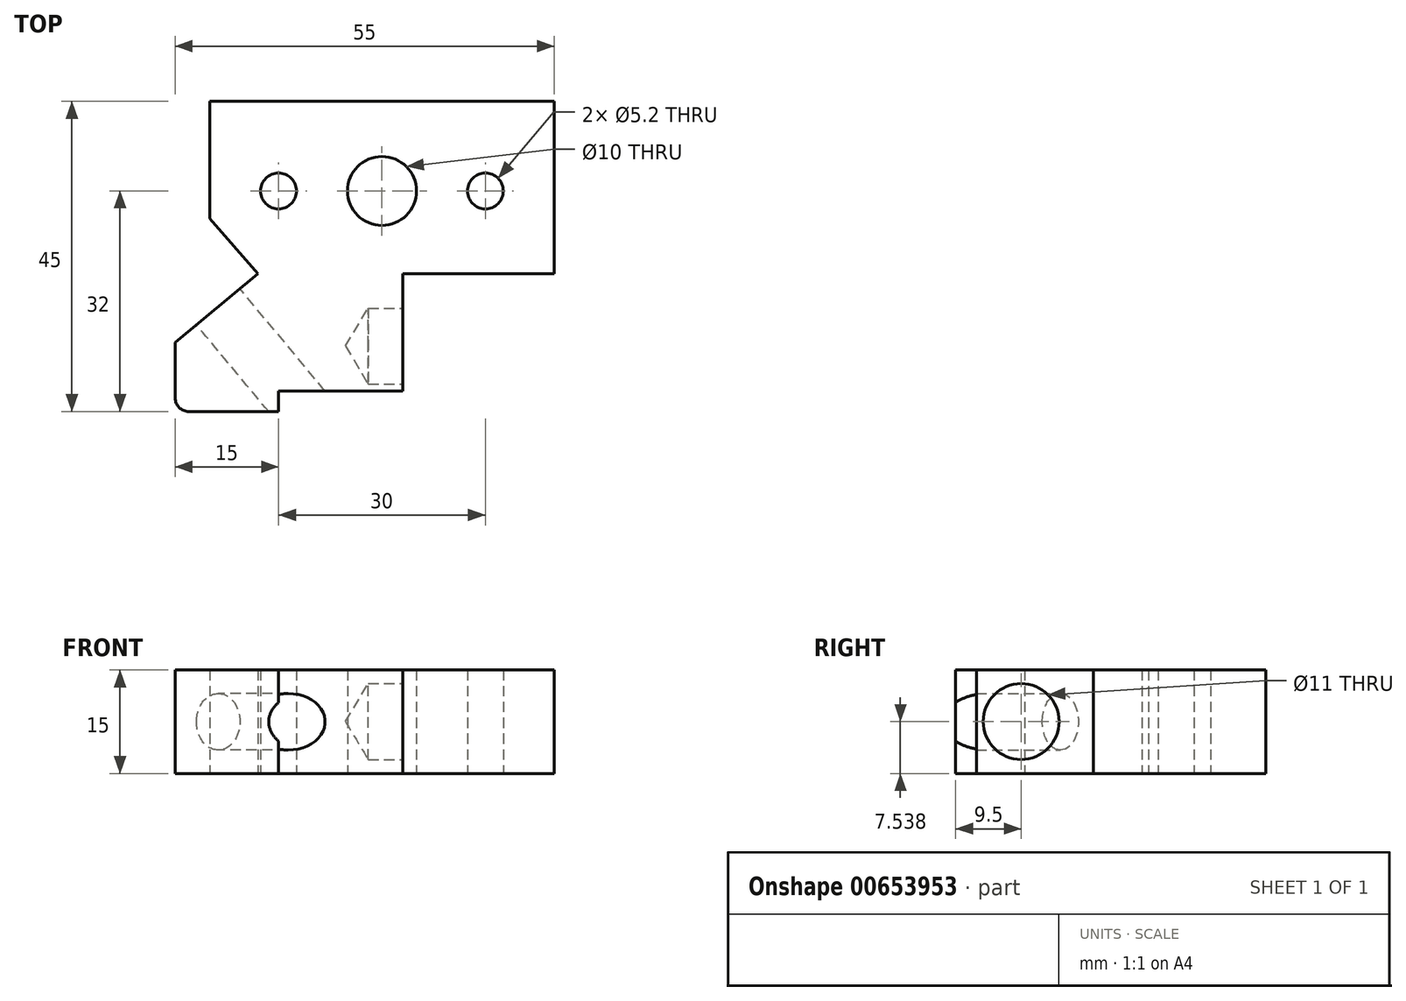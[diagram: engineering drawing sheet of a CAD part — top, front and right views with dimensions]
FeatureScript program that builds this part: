
annotation { "Feature Type Name" : "Feature", "Feature Type Description" : "" }
export const myFeature = defineFeature(function(context is Context, id is Id, definition is map)
    precondition{}
    {
        {
            var Q0;
            Q0=qCreatedBy(makeId("Top.planeOp"),FACE);
            var sketch = newSketch(context, id + "F0", { "sketchPlane" : qUnion([Q0])});
            skLineSegment(sketch, "E0.bottom", {"start": v(-25, 13) * mm, "end": v(25, 13) * mm});
            skLineSegment(sketch, "E0.left", {"start": v(-25, 13) * mm, "end": v(-25, -4) * mm});
            skLineSegment(sketch, "E0.right", {"start": v(25, 13) * mm, "end": v(25, -12) * mm});
            skPoint(sketch, "E1.end.orphan", {"position": v(0, -23.39) * mm});
            skLineSegment(sketch, "E2", {"start": v(25, -12) * mm, "end": v(3, -12) * mm});
            skLineSegment(sketch, "E3", {"start": v(3, -12) * mm, "end": v(3, -29) * mm});
            skLineSegment(sketch, "E4", {"start": v(3, -29) * mm, "end": v(-15, -29) * mm});
            skLineSegment(sketch, "E5", {"start": v(-15, -29) * mm, "end": v(-15, -32) * mm});
            skLineSegment(sketch, "E6", {"start": v(-15, -32) * mm, "end": v(-28, -32) * mm});
            skLineSegment(sketch, "E7", {"start": v(-30, -30) * mm, "end": v(-30, -22) * mm});
            skLineSegment(sketch, "E8", {"start": v(-30, -22) * mm, "end": v(-18, -12) * mm});
            skLineSegment(sketch, "E9", {"start": v(-18, -12) * mm, "end": v(-25, -4) * mm});
            skPoint(sketch, "E10", {"position": v(15, 0) * mm});
            skPoint(sketch, "E11", {"position": v(0, 0) * mm});
            skPoint(sketch, "E12", {"position": v(-15, 0) * mm});
            skPoint(sketch, "E13.visualSharp", {"position": v(-30, -32) * mm});
            skArc(sketch, "E13.filletArc", {"start": v(-30, -30) * mm, "mid": v(-29.41, -31.41) * mm, "end": v(-28, -32) * mm});
            skSolve(sketch);
        }
        {
            var Q0;
            Q0=makeQuery(id+"F0.imprint","IMPRINT",FACE,{"disambiguationData":[TD([[makeQuery(id+"F0.imprint","IMPRINT",EDGE,{"derivedFrom":sQuery(id+"F0.wireOp",EDGE,"E0.bottom")}),-1.0]])]});
            extrude(context, id + "F1", {"entities" : qUnion([Q0]), "depth" : 15 * mm, "offsetDistance" : 25 * mm});
        }
        {
            var Q0;
            Q0=sQuery(id+"F0.wireOp",VERTEX,"E12");
            var Q1;
            Q1=sQuery(id+"F0.wireOp",VERTEX,"E10");
            var Q2;
            Q2=makeQuery(id+"F1.opExtrude","SWEPT_BODY",BODY,{"disambiguationData":[OSD([sQuery(id+"F0.wireOp",EDGE,"E0.bottom"),sQuery(id+"F0.wireOp",EDGE,"E0.left"),sQuery(id+"F0.wireOp",EDGE,"E0.right"),sQuery(id+"F0.wireOp",EDGE,"E2"),sQuery(id+"F0.wireOp",EDGE,"E3"),sQuery(id+"F0.wireOp",EDGE,"E4"),sQuery(id+"F0.wireOp",EDGE,"E5"),sQuery(id+"F0.wireOp",EDGE,"E6"),sQuery(id+"F0.wireOp",EDGE,"E7"),sQuery(id+"F0.wireOp",EDGE,"E8"),sQuery(id+"F0.wireOp",EDGE,"E9")])]});
            hole(context, id + "F2", {"style" : HoleStyle.SIMPLE, "endStyle" : HoleEndStyle.THROUGH, "oppositeDirection" : true, "holeDiameter" : 5.2 * mm, "majorDiameter" : 5 * mm, "isTappedThrough" : true, "tappedDepth" : 12 * mm, "tapClearance" : 3, "locations" : qUnion([Q0, Q1]), "scope" : qUnion([Q2])});
        }
        {
            var Q0;
            Q0=sQuery(id+"F0.wireOp",VERTEX,"E11");
            var Q1;
            Q1=makeQuery(id+"F1.opExtrude","SWEPT_BODY",BODY,{"disambiguationData":[OSD([sQuery(id+"F0.wireOp",EDGE,"E0.bottom"),sQuery(id+"F0.wireOp",EDGE,"E0.left"),sQuery(id+"F0.wireOp",EDGE,"E0.right"),sQuery(id+"F0.wireOp",EDGE,"E2"),sQuery(id+"F0.wireOp",EDGE,"E3"),sQuery(id+"F0.wireOp",EDGE,"E4"),sQuery(id+"F0.wireOp",EDGE,"E5"),sQuery(id+"F0.wireOp",EDGE,"E6"),sQuery(id+"F0.wireOp",EDGE,"E7"),sQuery(id+"F0.wireOp",EDGE,"E8"),sQuery(id+"F0.wireOp",EDGE,"E9")])]});
            hole(context, id + "F3", {"style" : HoleStyle.SIMPLE, "endStyle" : HoleEndStyle.THROUGH, "oppositeDirection" : true, "holeDiameter" : 10 * mm, "majorDiameter" : 5 * mm, "isTappedThrough" : true, "tappedDepth" : 12 * mm, "tapClearance" : 3, "locations" : qUnion([Q0]), "scope" : qUnion([Q1])});
        }
        {
            var Q0;
            Q0=makeQuery(id+"F1.opExtrude","SWEPT_FACE",FACE,{"disambiguationData":[OSD([sQuery(id+"F0.wireOp",EDGE,"E8")])]});
            var sketch = newSketch(context, id + "F4", { "sketchPlane" : qUnion([Q0])});
            skPoint(sketch, "E14", {"position": v(29.01, 7.5) * mm});
            skSolve(sketch);
        }
        {
            var Q0;
            Q0=sQuery(id+"F4.wireOp",VERTEX,"E14");
            var Q1;
            Q1=makeQuery(id+"F1.opExtrude","SWEPT_BODY",BODY,{"disambiguationData":[OSD([sQuery(id+"F0.wireOp",EDGE,"E0.bottom"),sQuery(id+"F0.wireOp",EDGE,"E0.left"),sQuery(id+"F0.wireOp",EDGE,"E0.right"),sQuery(id+"F0.wireOp",EDGE,"E2"),sQuery(id+"F0.wireOp",EDGE,"E3"),sQuery(id+"F0.wireOp",EDGE,"E4"),sQuery(id+"F0.wireOp",EDGE,"E5"),sQuery(id+"F0.wireOp",EDGE,"E6"),sQuery(id+"F0.wireOp",EDGE,"E7"),sQuery(id+"F0.wireOp",EDGE,"E8"),sQuery(id+"F0.wireOp",EDGE,"E9")])]});
            hole(context, id + "F5", {"style" : HoleStyle.SIMPLE, "endStyle" : HoleEndStyle.THROUGH, "standardTappedOrClearance" : lookupTablePath({ "standard" : "ISO", "size" : "8.2", "type" : "Drilled" }), "standardBlindInLast" : lookupTablePath({ "standard" : "ISO", "size" : "8.2", "type" : "Drilled" }), "holeDiameter" : 8.2 * mm, "majorDiameter" : 5 * mm, "isTappedThrough" : true, "tappedDepth" : 12 * mm, "tapClearance" : 3, "locations" : qUnion([Q0]), "scope" : qUnion([Q1])});
        }
        {
            var Q0;
            Q0=makeQuery(id+"F1.opExtrude","SWEPT_FACE",FACE,{"disambiguationData":[OSD([sQuery(id+"F0.wireOp",EDGE,"E3")])]});
            var sketch = newSketch(context, id + "F6", { "sketchPlane" : qUnion([Q0])});
            skPoint(sketch, "E15", {"position": v(-22.5, 7.54) * mm});
            skSolve(sketch);
        }
        {
            var Q0;
            Q0=sQuery(id+"F6.wireOp",VERTEX,"E15");
            var Q1;
            Q1=makeQuery(id+"F1.opExtrude","SWEPT_BODY",BODY,{"disambiguationData":[OSD([sQuery(id+"F0.wireOp",EDGE,"E0.bottom"),sQuery(id+"F0.wireOp",EDGE,"E0.left"),sQuery(id+"F0.wireOp",EDGE,"E0.right"),sQuery(id+"F0.wireOp",EDGE,"E2"),sQuery(id+"F0.wireOp",EDGE,"E3"),sQuery(id+"F0.wireOp",EDGE,"E4"),sQuery(id+"F0.wireOp",EDGE,"E5"),sQuery(id+"F0.wireOp",EDGE,"E6"),sQuery(id+"F0.wireOp",EDGE,"E7"),sQuery(id+"F0.wireOp",EDGE,"E8"),sQuery(id+"F0.wireOp",EDGE,"E9")])]});
            hole(context, id + "F7", {"style" : HoleStyle.SIMPLE, "endStyle" : HoleEndStyle.BLIND, "holeDiameter" : 11 * mm, "majorDiameter" : 5 * mm, "holeDepth" : 5 * mm, "isTappedThrough" : true, "tappedDepth" : 2.6 * mm, "tapClearance" : 0, "locations" : qUnion([Q0]), "scope" : qUnion([Q1])});
        }
    });
